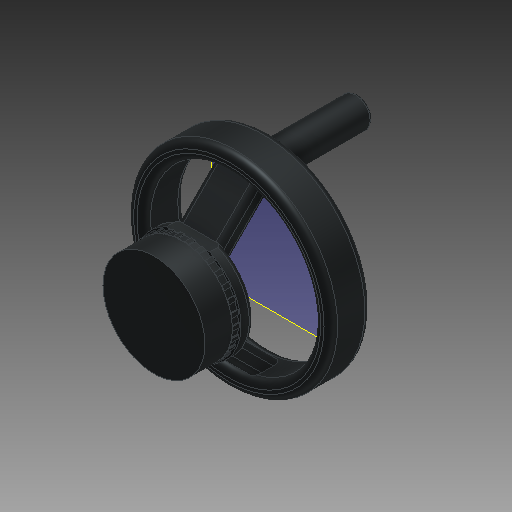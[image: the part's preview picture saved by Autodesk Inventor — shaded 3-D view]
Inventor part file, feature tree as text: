
AUTODESK INVENTOR PART (.ipt)
format: ipt  version: 2018 (Build 220112000, 112)  size: 559,616 bytes
history: native  units: mm
features: extrude x13, sketch x13, fillet x6, pattern_circular x1, chamfer x1, plane x1
ambient origin geometry x8: Origin, YZ Plane, XZ Plane, XY Plane, X Axis, Y Axis, Z Axis, Center Point
bodies: Solid1 (feature_tree)
feature tree (35):
  extrude  "Extrusion1"  Depth=20.0mm TaperAngle=0.0deg
  extrude  "Extrusion2"  Depth=5.0mm TaperAngle=0.0deg
  extrude  "Extrusion3"  Depth=5.0mm
  pattern_circular  "Circular Pattern1"  Count=30 Angle=360.0deg
  extrude  "Extrusion4"  Depth=10.0mm TaperAngle=0.0deg
  extrude  "Extrusion5"  Depth=16.0mm
  extrude  "Extrusion6"  Depth=10.0mm
  chamfer  "Chamfer1"  Distance=10.0mm
  plane  "Work Plane1"
  extrude  "Extrusion7"  Depth=2.0mm
  fillet  "Fillet1"  Radius=150.0mm
  extrude  "Extrusion8"  Depth=5.0mm TaperAngle=0.0deg
  fillet  "Fillet2"  Radius=5.0mm
  extrude  "Extrusion9"  Depth=5.0mm
  fillet  "Fillet3"  Radius=62.25mm
  extrude  "Extrusion10"  Depth=5.0mm TaperAngle=0.0deg
  fillet  "Fillet4"  Radius=4.0mm
  extrude  "Extrusion11"  Depth=4.0mm
  fillet  "Fillet5"  Radius=22.0mm
  extrude  "Extrusion12"  Depth=2.0mm TaperAngle=0.0deg
  extrude  "Extrusion13"  Depth=2.0mm
  fillet  "Fillet6"  [1 undecoded]
  sketch  "Sketch1"  dims[d0=75.0mm d1=20.0mm d2=0.0mm]
  sketch  "Sketch2"  dims[d3=76.0mm d4=5.0mm d5=0.0mm]
  sketch  "Sketch3"  dims[d7=2.5mm d8=5.0mm]
  sketch  "Sketch4"  dims[d9=5.0mm d10=0.0mm d11=300.0mm d12=360.0deg]
  sketch  "Sketch5"  dims[d14=78.0mm d15=10.0mm d16=0.0mm]
  sketch  "Sketch6"  dims[d17=16.0mm d18=16.0mm]
  sketch  "Sketch7"  dims[d19=10.0mm d20=0.0mm d21=55.0mm d22=10.0mm d23=0.0mm]
  sketch  "Sketch8"  dims[d24=10.0mm d25=2.0mm d26=45.0deg d27=50.0mm d28=150.0mm]
  sketch  "Sketch9"  dims[d29=125.0mm d30=30.0mm d31=0.0mm d32=5.0mm]
  sketch  "Sketch10"  dims[d33=61.75mm d34=0.0mm d35=5.0mm d36=62.25mm d37=0.0mm]
  sketch  "Sketch11"  dims[d38=5.0mm d39=32.0mm d40=0.0mm d41=4.0mm]
  sketch  "Sketch12"  dims[d42=32.0mm d43=0.0mm d44=4.0mm d45=22.0mm]
  sketch  "Sketch13"  dims[d46=50.0mm d47=0.0mm d48=40.0mm d49=0.0mm d50=2.0mm]
note: 1 required parameter value undecoded (feature->parameter linkage not recoverable at this tier; creation-order binding heuristic only, values carry confidence <= 0.55)
